# Revit family: CLAGE_EWT-C
name_source: partatom
category: Allgemeines Modell
units: mm (PartAtom-declared; Revit-internal decimal feet)

## family parameters
Arbeitsebenenbasiert = Nein
Beim Laden mit Abzugskörper schneiden = Nein
Bemaßung runder Anschluss = Durchmesser verwenden
Beschriftungsausrichtung beibehalten = Nein
Gemeinsam genutzt = Nein
Immer vertikal = Ja
Kann Basisbauteil für Bewehrung sein = Nein
Raumberechnungspunkt = Nein
Teiletyp = Normal

## types (1)
- Norm
    Angeforderte Genauigkeit = Niedrig
    Bauteilnummer = CLAGE_EWT-C
    Beschreibung = EWT-C Einhand-Waschtischbatterie
    Bestandsnummer = 1100-04421
    Dichte = 8490,00 kg/m³
    Erstellungsdatum = 05.12.2023
    Firma = CLAGE GmbH
    Fläche = 0,04 m²
    Hersteller = CLAGE
    Konstruktionsstatus = 1
    Masse = 3,42 kg
    Material = Messing
    Modell = 1110-04421
    Thema = Armatur
    Titel = CLAGE EWT-C
    Volumen = 0,00 m³
    Vorgabe-Ansicht = 0 mm  [stored 0 ft]

note: [stored X ft] marks values corroborated as IEEE doubles in the binary element streams (Revit-internal decimal feet)
